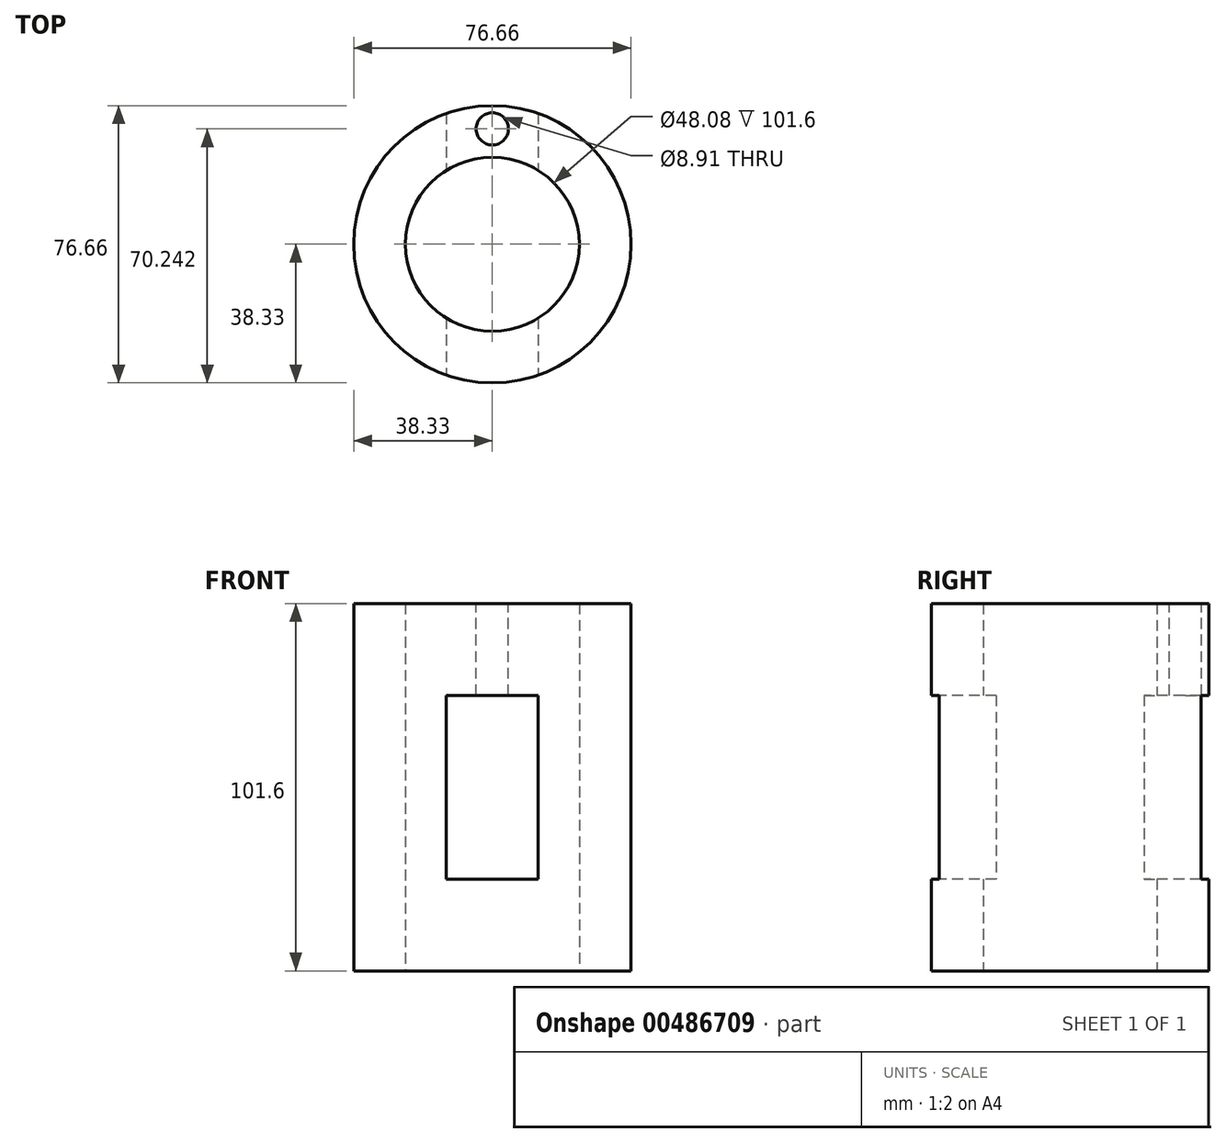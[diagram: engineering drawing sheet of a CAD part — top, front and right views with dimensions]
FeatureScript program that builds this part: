
annotation { "Feature Type Name" : "Feature", "Feature Type Description" : "" }
export const myFeature = defineFeature(function(context is Context, id is Id, definition is map)
    precondition{}
    {
        {
            var Q0;
            Q0=qCreatedBy(makeId("Top.planeOp"),FACE);
            var sketch = newSketch(context, id + "F0", { "sketchPlane" : qUnion([Q0])});
            skCircle(sketch, "E0", {"center": v(0, 0) * mm, "radius": 38.33 * mm});
            skCircle(sketch, "E1", {"center": v(0, 0) * mm, "radius": 24.04 * mm});
            skSolve(sketch);
        }
        {
            var Q0;
            Q0 = qSketchRegion(id + "F0", true);
            extrude(context, id + "F1", {"entities" : qUnion([Q0]), "depth" : 101.6 * mm});
        }
        {
            var Q0;
            Q0=qCreatedBy(makeId("Front.planeOp"),FACE);
            var sketch = newSketch(context, id + "F2", { "sketchPlane" : qUnion([Q0])});
            skLineSegment(sketch, "E2.bottom", {"start": v(-12.7, 25.4) * mm, "end": v(12.7, 25.4) * mm});
            skLineSegment(sketch, "E2.top", {"start": v(-12.7, 76.2) * mm, "end": v(12.7, 76.2) * mm});
            skLineSegment(sketch, "E2.left", {"start": v(-12.7, 25.4) * mm, "end": v(-12.7, 76.2) * mm});
            skLineSegment(sketch, "E2.right", {"start": v(12.7, 25.4) * mm, "end": v(12.7, 76.2) * mm});
            skSolve(sketch);
        }
        {
            var Q0;
            Q0 = qSketchRegion(id + "F2", true);
            extrude(context, id + "F3", {"entities" : qUnion([Q0]), "operationType" : NewBodyOperationType.REMOVE, "endBound" : BoundingType.THROUGH_ALL, "oppositeDirection" : true, "depth" : 25.4 * mm, "hasSecondDirection" : true, "secondDirectionBound" : SecondDirectionBoundingType.THROUGH_ALL, "secondDirectionOppositeDirection" : false, "secondDirectionDepth" : 25.4 * mm});
        }
        {
            var Q0;
            Q0=makeQuery(id+"F1.opExtrude","CAP_FACE",FACE,{"disambiguationData":[OSD([sQuery(id+"F0.wireOp",EDGE,"E0"),sQuery(id+"F0.wireOp",EDGE,"E1")])],"isStart":false});
            var sketch = newSketch(context, id + "F4", { "sketchPlane" : qUnion([Q0])});
            skCircle(sketch, "E3", {"center": v(0, 31.91) * mm, "radius": 4.46 * mm});
            skSolve(sketch);
        }
        {
            var Q0;
            Q0 = qSketchRegion(id + "F4", true);
            extrude(context, id + "F5", {"entities" : qUnion([Q0]), "operationType" : NewBodyOperationType.REMOVE, "endBound" : BoundingType.UP_TO_NEXT, "oppositeDirection" : true, "depth" : 25.4 * mm});
        }
    });
